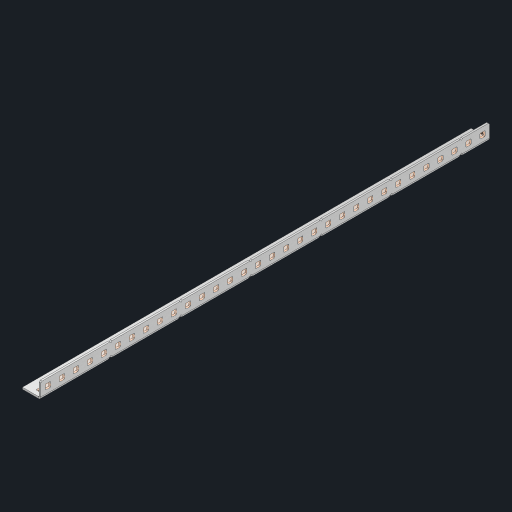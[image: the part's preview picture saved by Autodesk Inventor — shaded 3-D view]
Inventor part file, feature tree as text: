
AUTODESK INVENTOR PART (.ipt)
format: ipt  version: 2023 (Build 270158000, 158)  size: 1,005,568 bytes
history: native  units: in
note: dims shown in document units (in); Inventor stores cm internally (conversion verified against a paired STEP export)
features: other x69, extrude x63, sheet_metal_op x10, sketch x8, mirror x1, pattern_linear x1, chamfer x1
ambient origin geometry x8: Origin, YZ Plane, XZ Plane, XY Plane, X Axis, Y Axis, Z Axis, Center Point
bodies: Solid1 (feature_tree), Body (feature_tree)
feature tree (153):
  other  "Flange Pattern Plane"
  sheet_metal_op  "Flange Pattern"
  sheet_metal_op  "Body Pattern"
  other  "Arc Length"
  mirror  "Notch Mirror"
  pattern_linear  "Notch Pattern"  Spacing1=0.25in  [1 undecoded]
  chamfer  "End Chamfer"
  extrude  "Half Cut"  Depth=0.0625in
  sketch  "Sketch1"  dims[d0=1.5in]
  other  "Plate1"
  sketch  "Sketch2"  dims[d1=16.0in]
  other  "Plate2"
  sheet_metal_op  "Bend1"
  sheet_metal_op  "Corner1"
  sketch  "Sketch3"  dims[d2=0.0625in]
  other  "Flange Pattern Sketch"
  sketch  "Sketch7"  dims[d3=0.0625in]
  other  "Srf1"
  other  "Srf2"
  sketch  "Sketch8"  dims[d4=0.0312in]
  sketch  "Sketch9"  dims[d5=0.125in]
  other  "Srf91"
  sheet_metal_op  "Body Pattern Sketch"
  other  "Srf92"
  sketch  "Sketch13"  dims[d6=0.0625in]
  sketch  "Sketch14"  dims[d7=0.5in d8=90.0deg d9=0.0312in d10=0.25in d11=0.0625in d12=0.0625in d16=0.182in d17=0.02in d18=0.0625in d19=0.0in d20=0.25in d21=0.25in d46=0.172in d47=1.0in d48=0.0in d49=0.182in d50=0.02in d51=0.25in d52=0.25in d53=0.0625in d54=0.0in d55=0.172in d56=1.0in d57=0.0in d60=12.5984in d62=0.5in d63=0.3937in d65=0.5in d85=0.1473in d86=0.1782in d88=0.04in d89=0.0625in d90=0.0in d91=0.04in d92=0.0491in d95=2.5in d96=0.04in d97=0.25in d98=45.0deg d101=0.0in d102=2.497in d131=0.5in d132=12.5984in d134=0.5in d139=0.5in]
  other  "Srf856"
  other  "Srf1310"
  other  "Srf1311"
  other  "Srf1312"
  other  "Srf1376"
  other  "Srf1377"
  other  "Srf1728"
  other  "Srf1755"
  other  "Srf1878"
  other  "Srf1879"
  other  "Srf1880"
  other  "Srf1881"
  other  "Srf1882"
  other  "Srf1883"
  other  "Srf1884"
  other  "Srf1885"
  other  "Srf1886"
  other  "Srf1887"
  other  "Srf1888"
  other  "Srf1889"
  other  "Srf1890"
  other  "Srf1891"
  other  "Srf1892"
  other  "Srf1893"
  other  "Srf1894"
  other  "Srf1895"
  other  "Srf1896"
  other  "Srf1897"
  other  "Srf1898"
  other  "Srf1899"
  other  "Srf1900"
  other  "Srf1901"
  other  "Srf1902"
  other  "Srf1903"
  other  "Srf1942"
  other  "Srf1943"
  other  "Srf1944"
  other  "Srf1945"
  other  "Srf1946"
  other  "Srf1947"
  other  "Srf1948"
  other  "Srf1949"
  other  "Srf1950"
  other  "Srf1951"
  other  "Srf1952"
  other  "Srf1953"
  other  "Srf1954"
  other  "Srf1955"
  other  "Srf1956"
  other  "Srf1957"
  other  "Srf1958"
  other  "Srf1959"
  other  "Srf1960"
  other  "Srf1961"
  other  "Srf1962"
  other  "Srf1963"
  other  "Srf1964"
  other  "Srf1965"
  other  "Srf1966"
  other  "Srf1967"
  sheet_metal_op  "Flange Stamp"
  sheet_metal_op  "Flange Circle"
  sheet_metal_op  "Body Stamp"
  sheet_metal_op  "Body Circle"
  sheet_metal_op  "Notch"
  extrude  "ExtrusionSrf2"  Depth=0.0625in
  extrude  "ExtrusionSrf92"  Depth=0.5in
  extrude  "ExtrusionSrf856"  Depth=0.02in
  extrude  "ExtrusionSrf1310"  Depth=0.0625in
  extrude  "ExtrusionSrf1311"  TaperAngle=0.0deg  [1 undecoded]
  extrude  "ExtrusionSrf1312"  Depth=0.5in
  extrude  "ExtrusionSrf1376"  Depth=0.5in
  extrude  "ExtrusionSrf1377"  Depth=0.5in
  extrude  "ExtrusionSrf1728"  Depth=0.5in TaperAngle=0.0deg
  extrude  "ExtrusionSrf1755"  Depth=0.5in
  extrude  "ExtrusionSrf1878"  Depth=0.02in
  extrude  "ExtrusionSrf1879"  Depth=0.5in
  extrude  "ExtrusionSrf1880"  Depth=0.5in
  extrude  "ExtrusionSrf1881"  Depth=0.0625in
  extrude  "ExtrusionSrf1882"  TaperAngle=0.0deg  [1 undecoded]
  extrude  "ExtrusionSrf1883"  Depth=0.5in
  extrude  "ExtrusionSrf1884"  Depth=0.5in TaperAngle=0.0deg
  extrude  "ExtrusionSrf1885"  Depth=0.5in
  extrude  "ExtrusionSrf1886"  Depth=0.5in
  extrude  "ExtrusionSrf1887"  Depth=0.5in
  extrude  "ExtrusionSrf1888"  Depth=0.5in
  extrude  "ExtrusionSrf1889"  Depth=0.5in
  extrude  "ExtrusionSrf1890"  Depth=0.0625in
  extrude  "ExtrusionSrf1891"  TaperAngle=0.0deg  [1 undecoded]
  extrude  "ExtrusionSrf1892"  Depth=0.5in
  extrude  "ExtrusionSrf1893"  Depth=0.5in
  extrude  "ExtrusionSrf1894"  Depth=0.5in
  extrude  "ExtrusionSrf1895"  Depth=0.5in TaperAngle=45.0deg
  extrude  "ExtrusionSrf1896"  TaperAngle=0.0deg  [1 undecoded]
  extrude  "ExtrusionSrf1897"  Depth=0.5in
  extrude  "ExtrusionSrf1898"  Depth=0.5in
  extrude  "ExtrusionSrf1899"  Depth=0.5in
  extrude  "ExtrusionSrf1900"  Depth=0.5in
  extrude  "ExtrusionSrf1901"  Depth=0.5in
  extrude  "ExtrusionSrf1902"  [1 undecoded]
  extrude  "ExtrusionSrf1903"  [1 undecoded]
  extrude  "ExtrusionSrf1942"  [1 undecoded]
  extrude  "ExtrusionSrf1943"  [1 undecoded]
  extrude  "ExtrusionSrf1944"  [1 undecoded]
  extrude  "ExtrusionSrf1945"  [1 undecoded]
  extrude  "ExtrusionSrf1946"  [1 undecoded]
  extrude  "ExtrusionSrf1947"  [1 undecoded]
  extrude  "ExtrusionSrf1948"  [1 undecoded]
  extrude  "ExtrusionSrf1949"  [1 undecoded]
  extrude  "ExtrusionSrf1950"  [1 undecoded]
  extrude  "ExtrusionSrf1951"  [1 undecoded]
  extrude  "ExtrusionSrf1952"  [1 undecoded]
  extrude  "ExtrusionSrf1953"  [1 undecoded]
  extrude  "ExtrusionSrf1954"  [1 undecoded]
  extrude  "ExtrusionSrf1955"  [1 undecoded]
  extrude  "ExtrusionSrf1956"  [1 undecoded]
  extrude  "ExtrusionSrf1957"  [1 undecoded]
  extrude  "ExtrusionSrf1958"  [1 undecoded]
  extrude  "ExtrusionSrf1959"  [1 undecoded]
  extrude  "ExtrusionSrf1960"  [1 undecoded]
  extrude  "ExtrusionSrf1961"  [1 undecoded]
  extrude  "ExtrusionSrf1962"  [1 undecoded]
  extrude  "ExtrusionSrf1963"  [1 undecoded]
  extrude  "ExtrusionSrf1964"  [1 undecoded]
  extrude  "ExtrusionSrf1965"  [1 undecoded]
  extrude  "ExtrusionSrf1966"  [1 undecoded]
  extrude  "ExtrusionSrf1967"  [1 undecoded]
note: 33 required parameter values undecoded (feature->parameter linkage not recoverable at this tier; creation-order binding heuristic only, values carry confidence <= 0.55)
